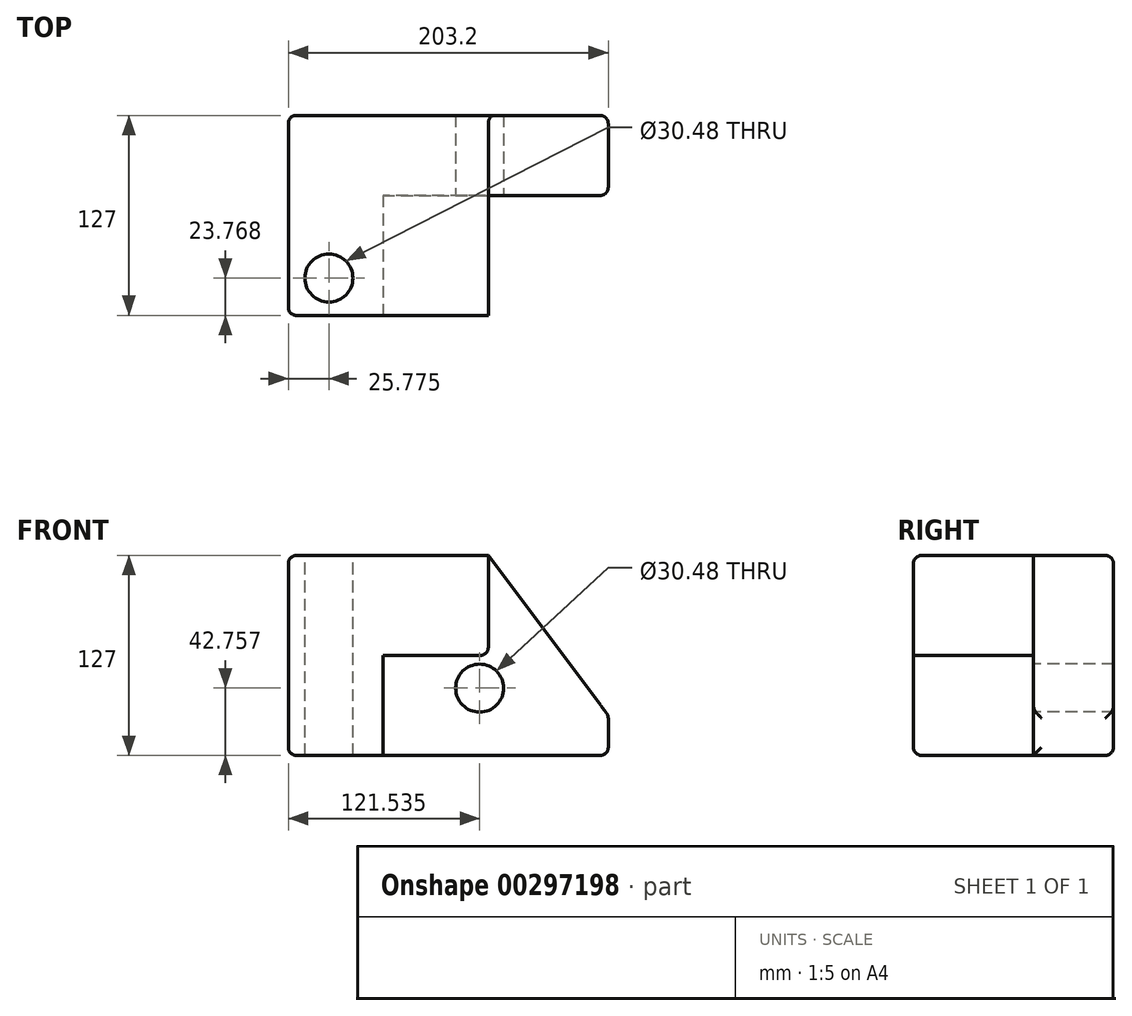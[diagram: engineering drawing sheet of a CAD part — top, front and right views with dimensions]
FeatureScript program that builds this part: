
annotation { "Feature Type Name" : "Feature", "Feature Type Description" : "" }
export const myFeature = defineFeature(function(context is Context, id is Id, definition is map)
    precondition{}
    {
        {
            var Q0;
            Q0=qCreatedBy(makeId("Front.planeOp"),FACE);
            var sketch = newSketch(context, id + "F0", { "sketchPlane" : qUnion([Q0])});
            skLineSegment(sketch, "E0.bottom", {"start": v(-101.6, 63.5) * mm, "end": v(101.6, 63.5) * mm});
            skLineSegment(sketch, "E0.top", {"start": v(-101.6, -63.5) * mm, "end": v(101.6, -63.5) * mm});
            skLineSegment(sketch, "E0.left", {"start": v(-101.6, 63.5) * mm, "end": v(-101.6, -63.5) * mm});
            skLineSegment(sketch, "E0.right", {"start": v(101.6, 63.5) * mm, "end": v(101.6, -63.5) * mm});
            skPoint(sketch, "E0.middle", {"position": v(0, 0) * mm});
            skSolve(sketch);
        }
        {
            var Q0;
            Q0 = qSketchRegion(id + "F0", true);
            extrude(context, id + "F1", {"entities" : qUnion([Q0]), "depth" : 127 * mm});
        }
        {
            var Q0;
            Q0=makeQuery(id+"F1.opExtrude","CAP_FACE",FACE,{"disambiguationData":[OSD([sQuery(id+"F0.wireOp",EDGE,"E0.bottom"),sQuery(id+"F0.wireOp",EDGE,"E0.top"),sQuery(id+"F0.wireOp",EDGE,"E0.left"),sQuery(id+"F0.wireOp",EDGE,"E0.right")])],"isStart":false});
            var sketch = newSketch(context, id + "F2", { "sketchPlane" : qUnion([Q0])});
            skLineSegment(sketch, "E1", {"start": v(-101.6, 63.5) * mm, "end": v(25.4, 63.5) * mm});
            skLineSegment(sketch, "E2", {"start": v(25.4, 63.5) * mm, "end": v(25.4, 0) * mm});
            skLineSegment(sketch, "E3", {"start": v(25.4, 0) * mm, "end": v(-41.49, 0) * mm});
            skLineSegment(sketch, "E4", {"start": v(-41.49, 0) * mm, "end": v(-41.49, -67.35) * mm});
            skSolve(sketch);
        }
        {
            var Q0;
            {var subQ2=sQuery(id+"F2.wireOp",EDGE,"E2");Q0=makeQuery(id+"F2.imprint","IMPRINT",FACE,{"disambiguationData":[TD([[makeQuery(id+"F2.imprint","IMPRINT",EDGE,{"derivedFrom":subQ2}),1.0]])]});}
            extrude(context, id + "F3", {"entities" : qUnion([Q0]), "operationType" : NewBodyOperationType.REMOVE, "oppositeDirection" : true, "depth" : 76.2 * mm});
        }
        {
            var Q0;
            Q0=makeQuery(id+"F1.opExtrude","SWEPT_EDGE",EDGE,{"disambiguationData":[OSD([sQuery(id+"F0.wireOp",EDGE,"E0.bottom"),sQuery(id+"F0.wireOp",EDGE,"E0.right")])]});
            chamfer(context, id + "F4", {"entities" : qUnion([Q0]), "chamferType" : ChamferType.TWO_OFFSETS, "width1" : 76.2 * mm, "oppositeDirection" : false, "width2" : 101.6 * mm, "tangentPropagation" : true});
        }
        {
            var Q0;
            Q0=makeQuery(id+"F1.opExtrude","CAP_EDGE",EDGE,{"disambiguationData":[OSD([sQuery(id+"F0.wireOp",EDGE,"E0.bottom")])],"isStart":false});
            var Q1;
            Q1=makeQuery(id+"F3.boolean.opBoolean","COPY",EDGE,{"derivedFrom":makeQuery(id+"F3.opExtrude","SWEPT_EDGE",EDGE,{"disambiguationData":[OSD([sQuery(id+"F0.wireOp",EDGE,"E0.bottom"),sQuery(id+"F2.wireOp",EDGE,"E1"),sQuery(id+"F2.wireOp",EDGE,"E2")])]})});
            var Q2;
            Q2=makeQuery(id+"F3.boolean.opBoolean","COPY",EDGE,{"derivedFrom":makeQuery(id+"F3.opExtrude","SWEPT_EDGE",EDGE,{"disambiguationData":[OSD([sQuery(id+"F2.wireOp",EDGE,"E2"),sQuery(id+"F2.wireOp",EDGE,"E3")])]})});
            var Q3;
            Q3=makeQuery(id+"F3.boolean.opBoolean","COPY",EDGE,{"derivedFrom":makeQuery(id+"F3.opExtrude","CAP_EDGE",EDGE,{"disambiguationData":[OSD([sQuery(id+"F2.wireOp",EDGE,"E3")])],"isStart":true})});
            var Q4;
            Q4=makeQuery(id+"F1.opExtrude","SWEPT_EDGE",EDGE,{"disambiguationData":[OSD([sQuery(id+"F0.wireOp",EDGE,"E0.bottom"),sQuery(id+"F0.wireOp",EDGE,"E0.left")])]});
            var Q5;
            Q5=makeQuery(id+"F3.boolean.opBoolean","COPY",EDGE,{"derivedFrom":makeQuery(id+"F3.opExtrude","CAP_EDGE",EDGE,{"disambiguationData":[OSD([sQuery(id+"F2.wireOp",EDGE,"E4")])],"isStart":true})});
            var Q6;
            Q6=makeQuery(id+"F3.boolean.opBoolean","COPY",EDGE,{"derivedFrom":makeQuery(id+"F3.opExtrude","SWEPT_EDGE",EDGE,{"disambiguationData":[OSD([sQuery(id+"F0.wireOp",EDGE,"E0.top"),sQuery(id+"F2.wireOp",EDGE,"E4")])]})});
            var Q7;
            Q7=makeQuery(id+"F1.opExtrude","CAP_EDGE",EDGE,{"disambiguationData":[OSD([sQuery(id+"F0.wireOp",EDGE,"E0.top")])],"isStart":false});
            var Q8;
            Q8=makeQuery(id+"F3.boolean.opBoolean","COPY",EDGE,{"derivedFrom":makeQuery(id+"F3.opExtrude","CAP_EDGE",EDGE,{"disambiguationData":[OSD([sQuery(id+"F0.wireOp",EDGE,"E0.top")])],"isStart":false})});
            var Q9;
            Q9=makeQuery(id+"F1.opExtrude","SWEPT_EDGE",EDGE,{"disambiguationData":[OSD([sQuery(id+"F0.wireOp",EDGE,"E0.top"),sQuery(id+"F0.wireOp",EDGE,"E0.right")])]});
            var Q10;
            Q10=makeQuery(id+"F3.boolean.opBoolean","COPY",EDGE,{"derivedFrom":makeQuery(id+"F3.opExtrude","CAP_EDGE",EDGE,{"disambiguationData":[OSD([sQuery(id+"F0.wireOp",EDGE,"E0.right")])],"isStart":false})});
            var Q11;
            Q11=makeQuery(id+"F1.opExtrude","SWEPT_FACE",FACE,{"disambiguationData":[OSD([sQuery(id+"F0.wireOp",EDGE,"E0.right")])]});
            var Q12;
            Q12=makeQuery(id+"F1.opExtrude","CAP_EDGE",EDGE,{"disambiguationData":[OSD([sQuery(id+"F0.wireOp",EDGE,"E0.right")])],"isStart":true});
            var Q13;
            Q13=makeQuery(id+"F1.opExtrude","CAP_EDGE",EDGE,{"disambiguationData":[OSD([sQuery(id+"F0.wireOp",EDGE,"E0.top")])],"isStart":true});
            var Q14;
            Q14=makeQuery(id+"F1.opExtrude","CAP_EDGE",EDGE,{"disambiguationData":[OSD([sQuery(id+"F0.wireOp",EDGE,"E0.left")])],"isStart":true});
            var Q15;
            Q15=makeQuery(id+"F1.opExtrude","SWEPT_EDGE",EDGE,{"disambiguationData":[OSD([sQuery(id+"F0.wireOp",EDGE,"E0.top"),sQuery(id+"F0.wireOp",EDGE,"E0.left")])]});
            var Q16;
            Q16=makeQuery(id+"F3.boolean.opBoolean","COPY",EDGE,{"derivedFrom":makeQuery(id+"F3.opExtrude","CAP_EDGE",EDGE,{"disambiguationData":[OSD([sQuery(id+"F2.wireOp",EDGE,"E2")])],"isStart":true})});
            var Q17;
            Q17=makeQuery(id+"F1.opExtrude","CAP_EDGE",EDGE,{"disambiguationData":[OSD([sQuery(id+"F0.wireOp",EDGE,"E0.left")])],"isStart":false});
            var Q18;
            Q18=makeQuery(id+"F1.opExtrude","CAP_EDGE",EDGE,{"disambiguationData":[OSD([sQuery(id+"F0.wireOp",EDGE,"E0.bottom")])],"isStart":true});
            fillet(context, id + "F5", {"entities" : qUnion([Q0, Q1, Q2, Q3, Q4, Q5, Q6, Q7, Q8, Q9, Q10, Q11, Q12, Q13, Q14, Q15, Q16, Q17, Q18]), "radius" : 5.08 * mm, "tangentPropagation" : true, "allowEdgeOverflow" : false});
        }
        {
            var Q0;
            Q0=qCreatedBy(makeId("Front.planeOp"),FACE);
            var sketch = newSketch(context, id + "F6", { "sketchPlane" : qUnion([Q0])});
            skCircle(sketch, "E5", {"center": v(19.94, -20.74) * mm, "radius": 15.24 * mm});
            skSolve(sketch);
        }
        {
            var Q0;
            Q0=makeQuery(id+"F6.imprint","IMPRINT",FACE,{"disambiguationData":[TD([[makeQuery(id+"F6.imprint","IMPRINT",EDGE,{"derivedFrom":sQuery(id+"F6.wireOp",EDGE,"E5")}),1.0]])]});
            extrude(context, id + "F7", {"entities" : qUnion([Q0]), "operationType" : NewBodyOperationType.REMOVE, "oppositeDirection" : true, "depth" : 25.4 * mm, "hasSecondDirection" : true, "secondDirectionOppositeDirection" : false, "secondDirectionDepth" : 76.2 * mm});
        }
        {
            var Q0;
            Q0=makeQuery(id+"F1.opExtrude","SWEPT_FACE",FACE,{"disambiguationData":[OSD([sQuery(id+"F0.wireOp",EDGE,"E0.bottom")])]});
            var sketch = newSketch(context, id + "F8", { "sketchPlane" : qUnion([Q0])});
            skCircle(sketch, "E6", {"center": v(-75.82, -103.23) * mm, "radius": 15.24 * mm});
            skSolve(sketch);
        }
        {
            var Q0;
            Q0=makeQuery(id+"F8.imprint","IMPRINT",FACE,{"disambiguationData":[TD([[makeQuery(id+"F8.imprint","IMPRINT",EDGE,{"derivedFrom":sQuery(id+"F8.wireOp",EDGE,"E6")}),1.0]])]});
            extrude(context, id + "F9", {"entities" : qUnion([Q0]), "operationType" : NewBodyOperationType.REMOVE, "oppositeDirection" : true, "depth" : 254 * mm, "hasSecondDirection" : true, "secondDirectionOppositeDirection" : false, "secondDirectionDepth" : 254 * mm});
        }
    });
